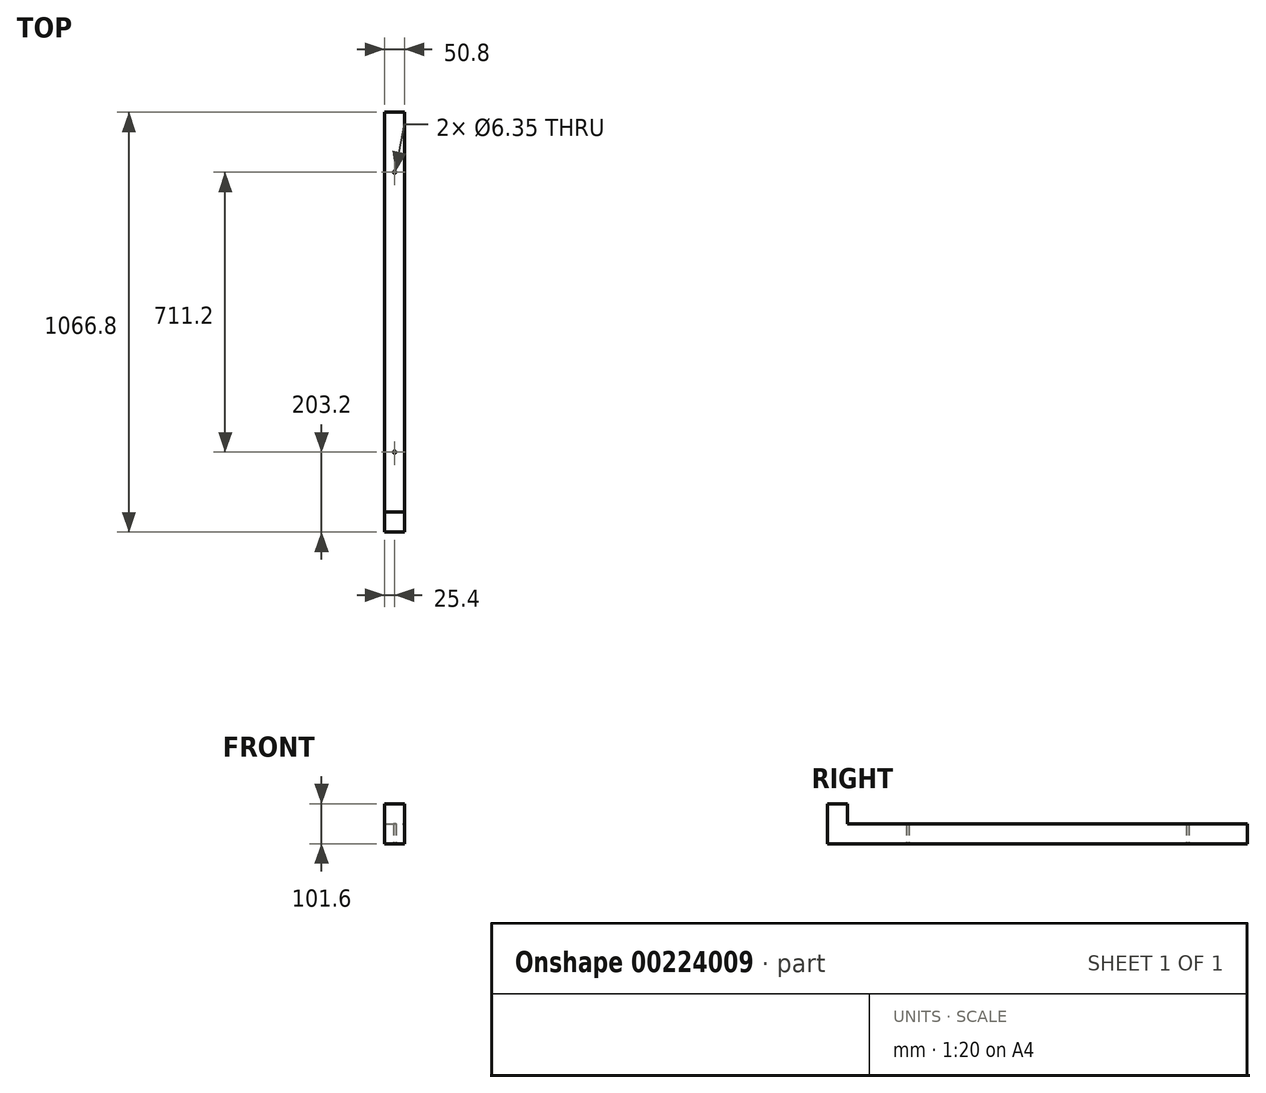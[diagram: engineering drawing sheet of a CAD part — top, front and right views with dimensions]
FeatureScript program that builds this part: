
annotation { "Feature Type Name" : "Feature", "Feature Type Description" : "" }
export const myFeature = defineFeature(function(context is Context, id is Id, definition is map)
    precondition{}
    {
        {
            var Q0;
            Q0=qCreatedBy(makeId("Top.planeOp"),FACE);
            var sketch = newSketch(context, id + "F0", { "sketchPlane" : qUnion([Q0])});
            skLineSegment(sketch, "E0.bottom", {"start": v(0, 0) * mm, "end": v(50.8, 0) * mm});
            skLineSegment(sketch, "E0.top", {"start": v(0, 1016) * mm, "end": v(50.8, 1016) * mm});
            skLineSegment(sketch, "E0.left", {"start": v(0, 0) * mm, "end": v(0, 1016) * mm});
            skLineSegment(sketch, "E0.right", {"start": v(50.8, 0) * mm, "end": v(50.8, 1016) * mm});
            skCircle(sketch, "E1", {"center": v(25.4, 152.4) * mm, "radius": 3.18 * mm});
            skCircle(sketch, "E2", {"center": v(25.4, 863.6) * mm, "radius": 3.18 * mm});
            skSolve(sketch);
        }
        {
            var Q0;
            Q0=makeQuery(id+"F0.imprint","IMPRINT",FACE,{"disambiguationData":[TD([[makeQuery(id+"F0.imprint","IMPRINT",EDGE,{"derivedFrom":sQuery(id+"F0.wireOp",EDGE,"E0.bottom")}),1.0]])]});
            extrude(context, id + "F1", {"entities" : qUnion([Q0]), "depth" : 50.8 * mm});
        }
        {
            var Q0;
            Q0=makeQuery(id+"F1.opExtrude","CAP_FACE",FACE,{"disambiguationData":[OSD([sQuery(id+"F0.wireOp",EDGE,"E0.bottom"),sQuery(id+"F0.wireOp",EDGE,"E0.top"),sQuery(id+"F0.wireOp",EDGE,"E0.left"),sQuery(id+"F0.wireOp",EDGE,"E0.right"),sQuery(id+"F0.wireOp",EDGE,"E1"),sQuery(id+"F0.wireOp",EDGE,"E2")])],"isStart":true});
            var sketch = newSketch(context, id + "F2", { "sketchPlane" : qUnion([Q0])});
            skLineSegment(sketch, "E3.bottom", {"start": v(0, 0) * mm, "end": v(50.8, 0) * mm});
            skLineSegment(sketch, "E3.top", {"start": v(0, 50.8) * mm, "end": v(50.8, 50.8) * mm});
            skLineSegment(sketch, "E3.left", {"start": v(0, 0) * mm, "end": v(0, 50.8) * mm});
            skLineSegment(sketch, "E3.right", {"start": v(50.8, 0) * mm, "end": v(50.8, 50.8) * mm});
            skSolve(sketch);
        }
        {
            var Q0;
            Q0=makeQuery(id+"F2.imprint","IMPRINT",FACE,{"disambiguationData":[TD([[makeQuery(id+"F2.imprint","IMPRINT",EDGE,{"derivedFrom":sQuery(id+"F2.wireOp",EDGE,"E3.bottom")}),1.0]])]});
            extrude(context, id + "F3", {"entities" : qUnion([Q0]), "operationType" : NewBodyOperationType.ADD, "oppositeDirection" : true, "depth" : 101.6 * mm});
        }
    });
